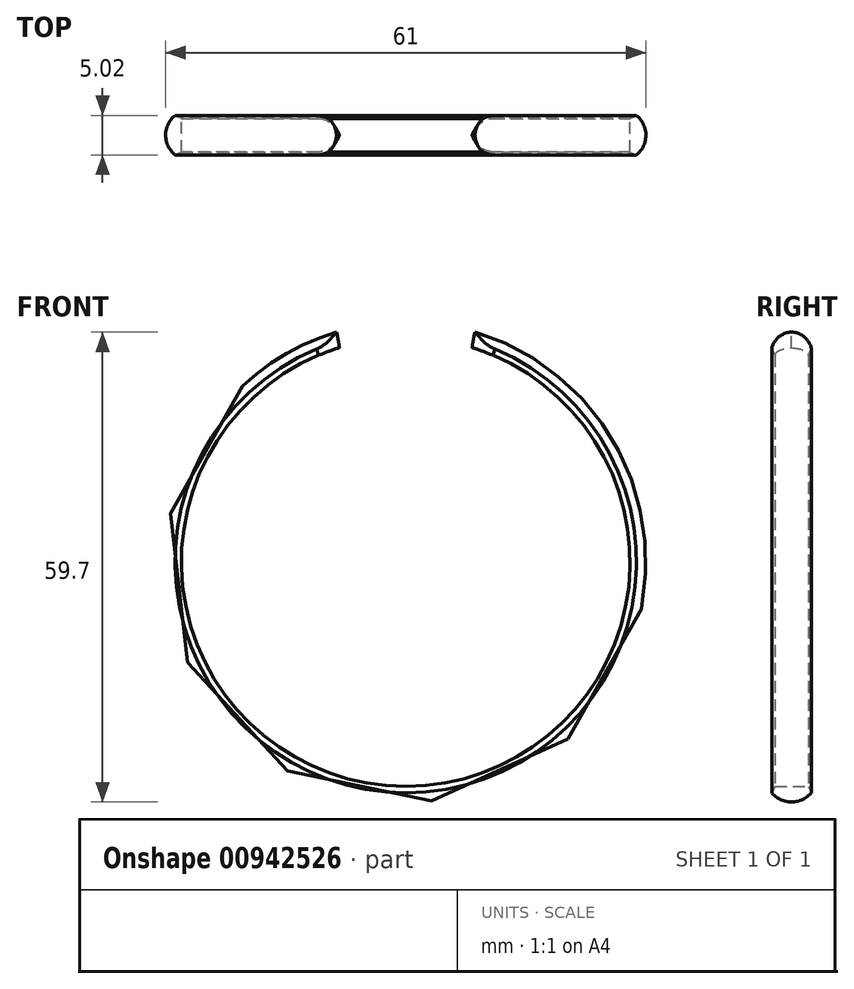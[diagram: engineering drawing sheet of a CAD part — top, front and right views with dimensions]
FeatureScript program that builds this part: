
annotation { "Feature Type Name" : "Feature", "Feature Type Description" : "" }
export const myFeature = defineFeature(function(context is Context, id is Id, definition is map)
    precondition{}
    {
        {
            var Q0;
            Q0=qCreatedBy(makeId("Front.planeOp"),FACE);
            var sketch = newSketch(context, id + "F0", { "sketchPlane" : qUnion([Q0])});
            skCircle(sketch, "E0", {"center": v(0, 0) * mm, "radius": 28.5 * mm});
            skSolve(sketch);
        }
        {
            var Q0;
            Q0=qCreatedBy(makeId("Right.planeOp"),FACE);
            var sketch = newSketch(context, id + "F1", { "sketchPlane" : qUnion([Q0])});
            skLineSegment(sketch, "E1", {"start": v(0, 28.5) * mm, "end": v(3, 28.5) * mm});
            skLineSegment(sketch, "E2.MirrorCS", {"start": v(0, 28.5) * mm, "end": v(-3, 28.5) * mm});
            skLineSegment(sketch, "E3", {"start": v(0, 28.5) * mm, "end": v(0, 30.5) * mm});
            skArc(sketch, "E4", {"start": v(0, 30.5) * mm, "mid": v(-1.8, 29.95) * mm, "end": v(-3, 28.5) * mm});
            skArc(sketch, "E5.MirrorCS", {"start": v(0, 30.5) * mm, "mid": v(1.8, 29.95) * mm, "end": v(3, 28.5) * mm});
            skSolve(sketch);
        }
        {
            var Q0;
            Q0=makeQuery(id+"F1.imprint","IMPRINT",FACE,{"disambiguationData":[TD([[makeQuery(id+"F1.imprint","IMPRINT",EDGE,{"derivedFrom":sQuery(id+"F1.wireOp",EDGE,"E2.MirrorCS")}),-1.0]])]});
            var Q1;
            Q1=makeQuery(id+"F1.imprint","IMPRINT",FACE,{"disambiguationData":[TD([[makeQuery(id+"F1.imprint","IMPRINT",EDGE,{"derivedFrom":sQuery(id+"F1.wireOp",EDGE,"E1")}),1.0]])]});
            var Q2;
            Q2=sQuery(id+"F0.wireOp",EDGE,"E0");
            revolve(context, id + "F2", {"surfaceOperationType" : NewSurfaceOperationType.NEW, "entities" : qUnion([Q0, Q1]), "axis" : qUnion([Q2]), "revolveType" : RevolveType.FULL});
        }
        {
            var Q0;
            Q0=qCreatedBy(makeId("Front.planeOp"),FACE);
            var sketch = newSketch(context, id + "F3", { "sketchPlane" : qUnion([Q0])});
            skLineSegment(sketch, "E6", {"start": v(0, 0) * mm, "end": v(-11.37, 37.83) * mm});
            skLineSegment(sketch, "E7", {"start": v(-11.37, 37.83) * mm, "end": v(0, 37.83) * mm});
            skLineSegment(sketch, "E8.MirrorCS", {"start": v(11.37, 37.83) * mm, "end": v(0, 37.83) * mm});
            skLineSegment(sketch, "E9.MirrorCS", {"start": v(0, 0) * mm, "end": v(11.37, 37.83) * mm});
            skSolve(sketch);
        }
        {
            var Q0;
            Q0=makeQuery(id+"F3.imprint","IMPRINT",FACE,{"disambiguationData":[TD([[makeQuery(id+"F3.imprint","IMPRINT",EDGE,{"derivedFrom":sQuery(id+"F3.wireOp",EDGE,"E6")}),-1.0]])]});
            extrude(context, id + "F4", {"entities" : qUnion([Q0]), "operationType" : NewBodyOperationType.REMOVE, "oppositeDirection" : true, "depth" : 25 * mm, "offsetDistance" : 25 * mm, "hasSecondDirection" : true, "secondDirectionOppositeDirection" : false, "secondDirectionDepth" : 25 * mm});
        }
        {
            var Q0;
            Q0=makeQuery(id+"F2.opRevolve","SWEPT_EDGE",EDGE,{"disambiguationData":[OSD([sQuery(id+"F1.wireOp",EDGE,"E1"),sQuery(id+"F1.wireOp",EDGE,"E5.MirrorCS")])]});
            var Q1;
            Q1=makeQuery(id+"F2.opRevolve","SWEPT_EDGE",EDGE,{"disambiguationData":[OSD([sQuery(id+"F1.wireOp",EDGE,"E2.MirrorCS"),sQuery(id+"F1.wireOp",EDGE,"E4")])]});
            chamfer(context, id + "F5", {"entities" : qUnion([Q0, Q1]), "width" : .5 * mm, "tangentPropagation" : true});
        }
        {
            var Q0;
            Q0=makeQuery(id+"F5.opChamfer","BLEND_EDGE",EDGE,{"blendedFrom":[makeQuery(id+"F2.opRevolve","SWEPT_EDGE",EDGE,{"disambiguationData":[OSD([sQuery(id+"F1.wireOp",EDGE,"E1"),sQuery(id+"F1.wireOp",EDGE,"E5.MirrorCS")])]}),makeQuery(id+"F4.boolean.opBoolean","COPY",FACE,{"derivedFrom":makeQuery(id+"F4.opExtrude","SWEPT_FACE",FACE,{"disambiguationData":[OSD([sQuery(id+"F3.wireOp",EDGE,"E9.MirrorCS")])]})})],"blendedInto":[makeQuery(id+"F4.boolean.opBoolean","COPY",FACE,{"derivedFrom":makeQuery(id+"F4.opExtrude","SWEPT_FACE",FACE,{"disambiguationData":[OSD([sQuery(id+"F3.wireOp",EDGE,"E9.MirrorCS")])]})})]});
            var Q1;
            Q1=makeQuery(id+"F5.opChamfer","BLEND_EDGE",EDGE,{"blendedFrom":[makeQuery(id+"F2.opRevolve","SWEPT_EDGE",EDGE,{"disambiguationData":[OSD([sQuery(id+"F1.wireOp",EDGE,"E2.MirrorCS"),sQuery(id+"F1.wireOp",EDGE,"E4")])]}),makeQuery(id+"F4.boolean.opBoolean","COPY",FACE,{"derivedFrom":makeQuery(id+"F4.opExtrude","SWEPT_FACE",FACE,{"disambiguationData":[OSD([sQuery(id+"F3.wireOp",EDGE,"E9.MirrorCS")])]})})],"blendedInto":[makeQuery(id+"F4.boolean.opBoolean","COPY",FACE,{"derivedFrom":makeQuery(id+"F4.opExtrude","SWEPT_FACE",FACE,{"disambiguationData":[OSD([sQuery(id+"F3.wireOp",EDGE,"E9.MirrorCS")])]})})]});
            var Q2;
            Q2=makeQuery(id+"F5.opChamfer","BLEND_EDGE",EDGE,{"blendedFrom":[makeQuery(id+"F2.opRevolve","SWEPT_EDGE",EDGE,{"disambiguationData":[OSD([sQuery(id+"F1.wireOp",EDGE,"E1"),sQuery(id+"F1.wireOp",EDGE,"E5.MirrorCS")])]}),makeQuery(id+"F4.boolean.opBoolean","COPY",FACE,{"derivedFrom":makeQuery(id+"F4.opExtrude","SWEPT_FACE",FACE,{"disambiguationData":[OSD([sQuery(id+"F3.wireOp",EDGE,"E6")])]})})],"blendedInto":[makeQuery(id+"F4.boolean.opBoolean","COPY",FACE,{"derivedFrom":makeQuery(id+"F4.opExtrude","SWEPT_FACE",FACE,{"disambiguationData":[OSD([sQuery(id+"F3.wireOp",EDGE,"E6")])]})})]});
            var Q3;
            Q3=makeQuery(id+"F5.opChamfer","BLEND_EDGE",EDGE,{"blendedFrom":[makeQuery(id+"F2.opRevolve","SWEPT_EDGE",EDGE,{"disambiguationData":[OSD([sQuery(id+"F1.wireOp",EDGE,"E2.MirrorCS"),sQuery(id+"F1.wireOp",EDGE,"E4")])]}),makeQuery(id+"F4.boolean.opBoolean","COPY",FACE,{"derivedFrom":makeQuery(id+"F4.opExtrude","SWEPT_FACE",FACE,{"disambiguationData":[OSD([sQuery(id+"F3.wireOp",EDGE,"E6")])]})})],"blendedInto":[makeQuery(id+"F4.boolean.opBoolean","COPY",FACE,{"derivedFrom":makeQuery(id+"F4.opExtrude","SWEPT_FACE",FACE,{"disambiguationData":[OSD([sQuery(id+"F3.wireOp",EDGE,"E6")])]})})]});
            fillet(context, id + "F6", {"entities" : qUnion([Q0, Q1, Q2, Q3]), "radius" : 3.2 * mm, "tangentPropagation" : true, "allowEdgeOverflow" : false});
        }
        {
            var Q0;
            Q0=qCreatedBy(makeId("Top.planeOp"),FACE);
            var sketch = newSketch(context, id + "F7", { "sketchPlane" : qUnion([Q0])});
            skLineSegment(sketch, "E10.bottom", {"start": v(16.07, -9.12) * mm, "end": v(16.07, -9.12) * mm});
            skLineSegment(sketch, "E10.top", {"start": v(16.07, -12.12) * mm, "end": v(16.07, -12.12) * mm});
            skLineSegment(sketch, "E10.left", {"start": v(-2.95, 1.04) * mm, "end": v(-2.95, -1.05) * mm});
            skLineSegment(sketch, "E10.right", {"start": v(-1.55, 1.04) * mm, "end": v(-1.55, -1.05) * mm});
            skLineSegment(sketch, "E11.bottom", {"start": v(18.32, -9.11) * mm, "end": v(18.32, -9.11) * mm});
            skLineSegment(sketch, "E11.top", {"start": v(18.32, -12.11) * mm, "end": v(18.32, -12.11) * mm});
            skLineSegment(sketch, "E11.left", {"start": v(-0.7, 1.05) * mm, "end": v(-0.7, -1.05) * mm});
            skLineSegment(sketch, "E11.right", {"start": v(0.7, 1.05) * mm, "end": v(0.7, -1.05) * mm});
            skLineSegment(sketch, "E12.bottom", {"start": v(20.58, -9.11) * mm, "end": v(20.58, -9.11) * mm});
            skLineSegment(sketch, "E12.top", {"start": v(20.58, -12.11) * mm, "end": v(20.58, -12.11) * mm});
            skLineSegment(sketch, "E12.left", {"start": v(1.55, 1.05) * mm, "end": v(1.55, -1.05) * mm});
            skLineSegment(sketch, "E12.right", {"start": v(2.95, 1.05) * mm, "end": v(2.95, -1.05) * mm});
            skPoint(sketch, "E13.visualSharp", {"position": v(-2.95, 1.74) * mm});
            skArc(sketch, "E13.filletArc", {"start": v(-2.25, 1.74) * mm, "mid": v(-2.75, 1.54) * mm, "end": v(-2.95, 1.04) * mm});
            skPoint(sketch, "E14.visualSharp", {"position": v(-1.55, 1.74) * mm});
            skArc(sketch, "E14.filletArc", {"start": v(-1.55, 1.04) * mm, "mid": v(-1.76, 1.54) * mm, "end": v(-2.25, 1.74) * mm});
            skPoint(sketch, "E15.visualSharp", {"position": v(-2.95, -1.75) * mm});
            skArc(sketch, "E15.filletArc", {"start": v(-2.95, -1.05) * mm, "mid": v(-2.75, -1.54) * mm, "end": v(-2.25, -1.75) * mm});
            skPoint(sketch, "E16.visualSharp", {"position": v(-1.55, -1.75) * mm});
            skArc(sketch, "E16.filletArc", {"start": v(-2.25, -1.75) * mm, "mid": v(-1.76, -1.54) * mm, "end": v(-1.55, -1.05) * mm});
            skPoint(sketch, "E17.visualSharp", {"position": v(-0.7, 1.75) * mm});
            skArc(sketch, "E17.filletArc", {"start": v(0, 1.75) * mm, "mid": v(-0.5, 1.54) * mm, "end": v(-0.7, 1.05) * mm});
            skPoint(sketch, "E18.visualSharp", {"position": v(0.7, 1.75) * mm});
            skArc(sketch, "E18.filletArc", {"start": v(0.7, 1.05) * mm, "mid": v(0.5, 1.54) * mm, "end": v(0, 1.75) * mm});
            skPoint(sketch, "E19.visualSharp", {"position": v(-0.7, -1.75) * mm});
            skArc(sketch, "E19.filletArc", {"start": v(-0.7, -1.05) * mm, "mid": v(-0.5, -1.54) * mm, "end": v(0, -1.75) * mm});
            skPoint(sketch, "E20.visualSharp", {"position": v(0.7, -1.75) * mm});
            skArc(sketch, "E20.filletArc", {"start": v(0, -1.75) * mm, "mid": v(0.5, -1.54) * mm, "end": v(0.7, -1.05) * mm});
            skPoint(sketch, "E21.visualSharp", {"position": v(1.55, 1.75) * mm});
            skArc(sketch, "E21.filletArc", {"start": v(2.25, 1.75) * mm, "mid": v(1.76, 1.54) * mm, "end": v(1.55, 1.05) * mm});
            skPoint(sketch, "E22.visualSharp", {"position": v(2.95, 1.75) * mm});
            skArc(sketch, "E22.filletArc", {"start": v(2.95, 1.05) * mm, "mid": v(2.75, 1.54) * mm, "end": v(2.25, 1.75) * mm});
            skPoint(sketch, "E23.visualSharp", {"position": v(2.95, -1.75) * mm});
            skArc(sketch, "E23.filletArc", {"start": v(2.25, -1.75) * mm, "mid": v(2.75, -1.54) * mm, "end": v(2.95, -1.05) * mm});
            skPoint(sketch, "E24.visualSharp", {"position": v(1.55, -1.75) * mm});
            skArc(sketch, "E24.filletArc", {"start": v(1.55, -1.05) * mm, "mid": v(1.76, -1.54) * mm, "end": v(2.25, -1.75) * mm});
            skLineSegment(sketch, "E25", {"start": v(0, 1.75) * mm, "end": v(0, -1.75) * mm, "construction": true});
            skPoint(sketch, "E26", {"position": v(0, 0) * mm});
            skCircle(sketch, "E27", {"center": v(0, 0) * mm, "radius": 0.5 * mm});
            skSolve(sketch);
        }
        {
            var Q0;
            Q0=makeQuery(id+"F7.imprint","IMPRINT",FACE,{"disambiguationData":[TD([[makeQuery(id+"F7.imprint","IMPRINT",EDGE,{"derivedFrom":sQuery(id+"F7.wireOp",EDGE,"E12.left")}),1.0]])]});
            var Q1;
            Q1=makeQuery(id+"F7.imprint","IMPRINT",FACE,{"disambiguationData":[TD([[makeQuery(id+"F7.imprint","IMPRINT",EDGE,{"derivedFrom":sQuery(id+"F7.wireOp",EDGE,"E11.left")}),1.0]])]});
            var Q2;
            Q2=makeQuery(id+"F7.imprint","IMPRINT",FACE,{"disambiguationData":[TD([[makeQuery(id+"F7.imprint","IMPRINT",EDGE,{"derivedFrom":sQuery(id+"F7.wireOp",EDGE,"E10.left")}),1.0]])]});
            extrude(context, id + "F8", {"entities" : qUnion([Q0, Q1, Q2]), "operationType" : NewBodyOperationType.REMOVE, "oppositeDirection" : true, "depth" : 9.3 * mm, "offsetDistance" : 25 * mm});
        }
        {
            var Q0;
            Q0=makeQuery(id+"F7.imprint","IMPRINT",FACE,{"disambiguationData":[TD([[makeQuery(id+"F7.imprint","IMPRINT",EDGE,{"derivedFrom":sQuery(id+"F7.wireOp",EDGE,"E27")}),1.0]])]});
            extrude(context, id + "F9", {"entities" : qUnion([Q0]), "operationType" : NewBodyOperationType.REMOVE, "oppositeDirection" : true, "depth" : 9.7 * mm, "offsetDistance" : 25 * mm});
        }
    });
